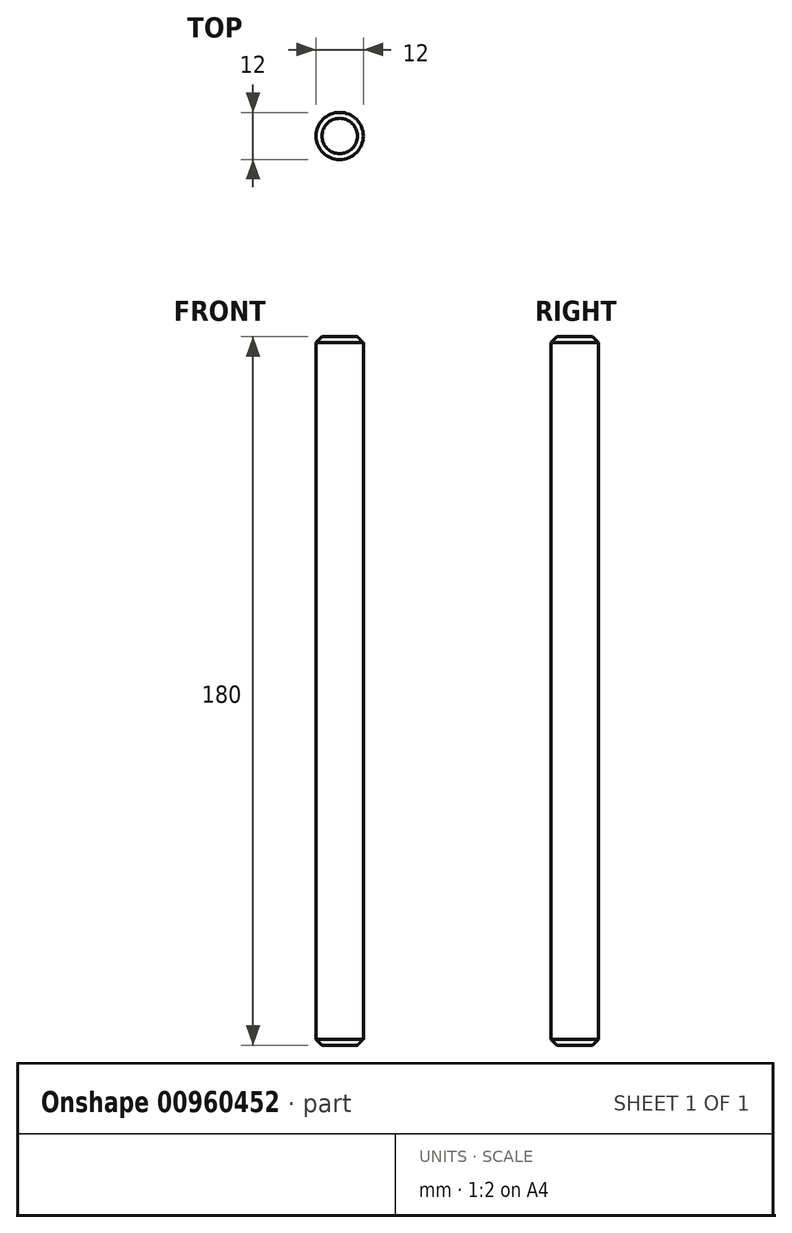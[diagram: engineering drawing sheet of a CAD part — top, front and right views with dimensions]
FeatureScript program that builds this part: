
annotation { "Feature Type Name" : "Feature", "Feature Type Description" : "" }
export const myFeature = defineFeature(function(context is Context, id is Id, definition is map)
    precondition{}
    {
        {
            var Q0;
            Q0=qCreatedBy(makeId("Top.planeOp"),FACE);
            var sketch = newSketch(context, id + "F0", { "sketchPlane" : qUnion([Q0])});
            skCircle(sketch, "E0", {"center": v(0, 0) * mm, "radius": 6 * mm});
            skSolve(sketch);
        }
        {
            var Q0;
            Q0 = qSketchRegion(id + "F0", true);
            var Q1;
            Q1=sQuery(id+"F0.wireOp",EDGE,"E0");
            extrude(context, id + "F1", {"entities" : qUnion([Q0]), "surfaceOperationType" : NewSurfaceOperationType.ADD, "surfaceEntities" : qUnion([Q1]), "depth" : 180 * mm, "offsetDistance" : 25 * mm});
        }
        {
            var Q0;
            Q0=makeQuery(id+"F1.opExtrude","CAP_FACE",FACE,{"disambiguationData":[OSD([sQuery(id+"F0.wireOp",EDGE,"E0")])],"isStart":true});
            var Q1;
            Q1=makeQuery(id+"F1.opExtrude","SWEPT_FACE",FACE,{"disambiguationData":[OSD([sQuery(id+"F0.wireOp",EDGE,"E0")])]});
            chamfer(context, id + "F2", {"entities" : qUnion([Q0, Q1]), "width" : 1.5 * mm, "tangentPropagation" : true});
        }
    });
